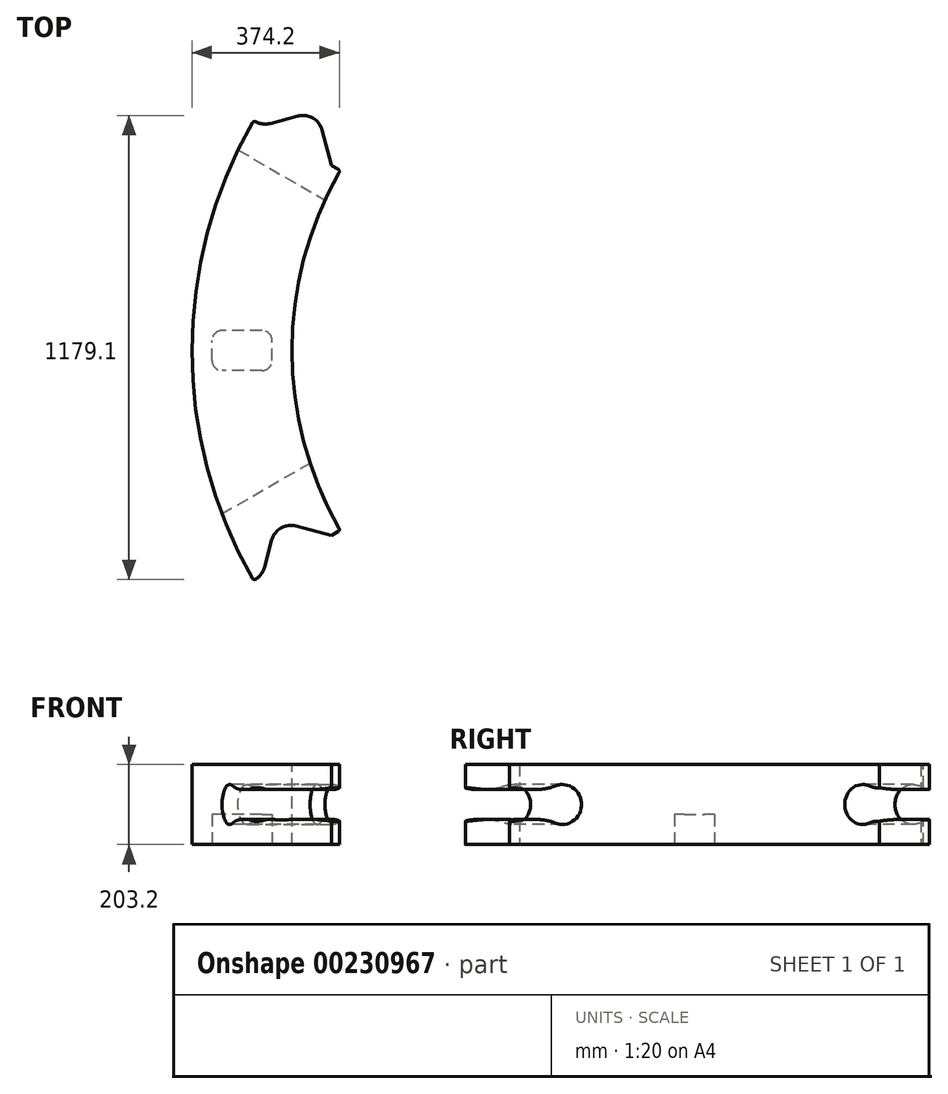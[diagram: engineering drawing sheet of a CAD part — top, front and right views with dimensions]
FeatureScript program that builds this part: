
annotation { "Feature Type Name" : "Feature", "Feature Type Description" : "" }
export const myFeature = defineFeature(function(context is Context, id is Id, definition is map)
    precondition{}
    {
        {
            var Q0;
            Q0=qCreatedBy(makeId("Front.planeOp"),FACE);
            var sketch = newSketch(context, id + "F0", { "sketchPlane" : qUnion([Q0])});
            skLineSegment(sketch, "E0.bottom", {"start": v(-1168.4, 101.6) * mm, "end": v(-914.4, 101.6) * mm});
            skLineSegment(sketch, "E0.top", {"start": v(-1168.4, -101.6) * mm, "end": v(-914.4, -101.6) * mm});
            skLineSegment(sketch, "E0.left", {"start": v(-1168.4, 101.6) * mm, "end": v(-1168.4, -101.6) * mm});
            skLineSegment(sketch, "E0.right", {"start": v(-914.4, 101.6) * mm, "end": v(-914.4, -101.6) * mm});
            skPoint(sketch, "E0.middle", {"position": v(-1041.4, 0) * mm});
            skLineSegment(sketch, "E1", {"start": v(0, 122.44) * mm, "end": v(0, -122.44) * mm, "construction": true});
            skSolve(sketch);
        }
        {
            var Q0;
            Q0=makeQuery(id+"F0.imprint","IMPRINT",FACE,{"disambiguationData":[TD([[makeQuery(id+"F0.imprint","IMPRINT",EDGE,{"derivedFrom":sQuery(id+"F0.wireOp",EDGE,"E0.bottom")}),-1.0]])]});
            var Q1;
            Q1=sQuery(id+"F0.wireOp",EDGE,"E1");
            revolve(context, id + "F1", {"entities" : qUnion([Q0]), "axis" : qUnion([Q1]), "revolveType" : RevolveType.SYMMETRIC, "angle" : 60 * degree});
        }
        {
            var Q0;
            Q0=makeQuery(id+"F1.opRevolve","SWEPT_FACE",FACE,{"disambiguationData":[OSD([sQuery(id+"F0.wireOp",EDGE,"E0.bottom")])]});
            var sketch = newSketch(context, id + "F2", { "sketchPlane" : qUnion([Q0])});
            skLineSegment(sketch, "E2", {"start": v(-989.87, 571.5) * mm, "end": v(-851.08, 608.69) * mm});
            skLineSegment(sketch, "E3", {"start": v(-851.08, 608.69) * mm, "end": v(-813.9, 469.9) * mm});
            skSolve(sketch);
        }
        {
            var Q0;
            Q0=makeQuery(id+"F2.imprint","IMPRINT",FACE,{"disambiguationData":[TD([[makeQuery(id+"F2.imprint","IMPRINT",EDGE,{"derivedFrom":sQuery(id+"F2.wireOp",EDGE,"E2")}),-1.0]])]});
            var Q1;
            Q1=makeQuery(id+"F1.opRevolve","SWEPT_FACE",FACE,{"disambiguationData":[OSD([sQuery(id+"F0.wireOp",EDGE,"E0.top")])]});
            extrude(context, id + "F3", {"entities" : qUnion([Q0]), "operationType" : NewBodyOperationType.ADD, "endBound" : BoundingType.UP_TO_SURFACE, "oppositeDirection" : true, "endBoundEntityFace" : qUnion([Q1]), "depth" : 25.4 * mm});
        }
        {
            var Q0;
            {var subQ0=sQuery(id+"F0.wireOp",EDGE,"E0.bottom");Q0=makeQuery(id+"F3.boolean.opBoolean","MERGE",FACE,{"derivedFrom":[makeQuery(id+"F1.opRevolve","SWEPT_FACE",FACE,{"disambiguationData":[OSD([subQ0])]}),makeQuery(id+"F3.opExtrude","CAP_FACE",FACE,{"disambiguationData":[OSD([subQ0,sQuery(id+"F2.wireOp",EDGE,"E2"),sQuery(id+"F2.wireOp",EDGE,"E3")])],"isStart":true})]});}
            var sketch = newSketch(context, id + "F4", { "sketchPlane" : qUnion([Q0])});
            skLineSegment(sketch, "E4", {"start": v(-989.87, -571.5) * mm, "end": v(-952.68, -432.71) * mm});
            skLineSegment(sketch, "E5", {"start": v(-952.68, -432.71) * mm, "end": v(-813.9, -469.9) * mm});
            skSolve(sketch);
        }
        {
            var Q0;
            Q0=qSketchRegion(id+"F4",true);
            var Q1;
            Q1=makeQuery(id+"F4.imprint","IMPRINT",FACE,{"disambiguationData":[TD([[makeQuery(id+"F4.imprint","IMPRINT",EDGE,{"derivedFrom":sQuery(id+"F4.wireOp",EDGE,"E4")}),-1.0]])]});
            var Q2;
            {var subQ0=sQuery(id+"F0.wireOp",EDGE,"E0.top");Q2=makeQuery(id+"F3.boolean.opBoolean","MERGE",FACE,{"derivedFrom":[makeQuery(id+"F1.opRevolve","SWEPT_FACE",FACE,{"disambiguationData":[OSD([subQ0])]}),makeQuery(id+"F3.opExtrude","CAP_FACE",FACE,{"disambiguationData":[OSD([subQ0])],"isStart":false})]});}
            extrude(context, id + "F5", {"entities" : qUnion([Q0, Q1]), "operationType" : NewBodyOperationType.REMOVE, "endBound" : BoundingType.UP_TO_SURFACE, "oppositeDirection" : true, "endBoundEntityFace" : qUnion([Q2]), "depth" : 25.4 * mm});
        }
        {
            var Q0;
            Q0=makeQuery(id+"F3.opExtrude","SWEPT_EDGE",EDGE,{"disambiguationData":[OSD([sQuery(id+"F2.wireOp",EDGE,"E2"),sQuery(id+"F2.wireOp",EDGE,"E3")])]});
            var Q1;
            Q1=makeQuery(id+"F3.opExtrude","SWEPT_FACE",FACE,{"disambiguationData":[OSD([sQuery(id+"F2.wireOp",EDGE,"E2")])]});
            cPlane(context, id + "F6", {"entities" : qUnion([Q0, Q1]), "cplaneType" : CPlaneType.LINE_ANGLE, "offset" : 25.4 * mm, "angle" : 45 * degree, "width" : 152.4 * mm, "height" : 152.4 * mm});
        }
        {
            var Q0;
            Q0=makeQuery(id+"F5.boolean.opBoolean","COPY",EDGE,{"derivedFrom":makeQuery(id+"F5.opExtrude","SWEPT_EDGE",EDGE,{"disambiguationData":[OSD([sQuery(id+"F4.wireOp",EDGE,"E4"),sQuery(id+"F4.wireOp",EDGE,"E5")])]})});
            var Q1;
            Q1=makeQuery(id+"F5.boolean.opBoolean","COPY",FACE,{"derivedFrom":makeQuery(id+"F5.opExtrude","SWEPT_FACE",FACE,{"disambiguationData":[OSD([sQuery(id+"F4.wireOp",EDGE,"E4")])]})});
            cPlane(context, id + "F7", {"entities" : qUnion([Q0, Q1]), "cplaneType" : CPlaneType.LINE_ANGLE, "offset" : 25.4 * mm, "angle" : 45 * degree, "width" : 152.4 * mm, "height" : 152.4 * mm});
        }
        {
            var Q0;
            Q0=qCreatedBy(id+"F6.planeOp",FACE);
            var sketch = newSketch(context, id + "F8", { "sketchPlane" : qUnion([Q0])});
            skArc(sketch, "E6", {"start": v(-15.92, 47.62) * mm, "mid": v(-84.4, 0) * mm, "end": v(-15.92, -47.63) * mm});
            skArc(sketch, "E7", {"start": v(117.52, -47.63) * mm, "mid": v(186, 0) * mm, "end": v(117.52, 47.62) * mm});
            skLineSegment(sketch, "E8", {"start": v(37.1, 38.1) * mm, "end": v(64.5, 38.1) * mm});
            skLineSegment(sketch, "E9", {"start": v(37.1, -38.1) * mm, "end": v(64.5, -38.1) * mm});
            skPoint(sketch, "E10.visualSharp", {"position": v(0, 38.1) * mm});
            skArc(sketch, "E10.filletArc", {"start": v(-15.92, 47.63) * mm, "mid": v(10.17, 40.5) * mm, "end": v(37.1, 38.1) * mm});
            skPoint(sketch, "E11.visualSharp", {"position": v(101.6, 38.1) * mm});
            skArc(sketch, "E11.filletArc", {"start": v(64.5, 38.1) * mm, "mid": v(91.43, 40.5) * mm, "end": v(117.52, 47.63) * mm});
            skPoint(sketch, "E12.visualSharp", {"position": v(101.6, -38.1) * mm});
            skArc(sketch, "E12.filletArc", {"start": v(117.52, -47.63) * mm, "mid": v(91.43, -40.5) * mm, "end": v(64.5, -38.1) * mm});
            skPoint(sketch, "E13.visualSharp", {"position": v(0, -38.1) * mm});
            skArc(sketch, "E13.filletArc", {"start": v(37.1, -38.1) * mm, "mid": v(10.17, -40.5) * mm, "end": v(-15.92, -47.63) * mm});
            skSolve(sketch);
        }
        {
            var Q0;
            Q0=qSketchRegion(id+"F8",true);
            extrude(context, id + "F9", {"entities" : qUnion([Q0]), "operationType" : NewBodyOperationType.REMOVE, "endBound" : BoundingType.SYMMETRIC, "oppositeDirection" : true, "depth" : 508 * mm});
        }
        {
            var Q0;
            Q0=qCreatedBy(id+"F7.planeOp",FACE);
            var sketch = newSketch(context, id + "F10", { "sketchPlane" : qUnion([Q0])});
            skArc(sketch, "E14", {"start": v(-117.52, 47.63) * mm, "mid": v(-186, 0) * mm, "end": v(-117.52, -47.63) * mm});
            skArc(sketch, "E15", {"start": v(15.92, -47.63) * mm, "mid": v(84.4, 0) * mm, "end": v(15.92, 47.63) * mm});
            skLineSegment(sketch, "E16", {"start": v(-37.1, 38.1) * mm, "end": v(-64.5, 38.1) * mm});
            skLineSegment(sketch, "E17", {"start": v(-37.1, -38.1) * mm, "end": v(-64.5, -38.1) * mm});
            skPoint(sketch, "E18.visualSharp", {"position": v(0, 38.1) * mm});
            skArc(sketch, "E18.filletArc", {"start": v(-37.1, 38.1) * mm, "mid": v(-10.17, 40.5) * mm, "end": v(15.92, 47.63) * mm});
            skPoint(sketch, "E19.visualSharp", {"position": v(-101.6, 38.1) * mm});
            skArc(sketch, "E19.filletArc", {"start": v(-117.52, 47.62) * mm, "mid": v(-91.43, 40.5) * mm, "end": v(-64.5, 38.1) * mm});
            skPoint(sketch, "E20.visualSharp", {"position": v(-101.6, -38.1) * mm});
            skArc(sketch, "E20.filletArc", {"start": v(-64.5, -38.1) * mm, "mid": v(-91.43, -40.5) * mm, "end": v(-117.52, -47.62) * mm});
            skPoint(sketch, "E21.visualSharp", {"position": v(0, -38.1) * mm});
            skArc(sketch, "E21.filletArc", {"start": v(15.92, -47.63) * mm, "mid": v(-10.17, -40.5) * mm, "end": v(-37.1, -38.1) * mm});
            skSolve(sketch);
        }
        {
            var Q0;
            Q0=qSketchRegion(id+"F10",true);
            extrude(context, id + "F11", {"entities" : qUnion([Q0]), "operationType" : NewBodyOperationType.REMOVE, "endBound" : BoundingType.SYMMETRIC, "oppositeDirection" : true, "depth" : 508 * mm});
        }
        {
            var Q0;
            {var subQ0=sQuery(id+"F0.wireOp",EDGE,"E0.top");Q0=makeQuery(id+"F3.boolean.opBoolean","MERGE",FACE,{"derivedFrom":[makeQuery(id+"F1.opRevolve","SWEPT_FACE",FACE,{"disambiguationData":[OSD([subQ0])]}),makeQuery(id+"F3.opExtrude","CAP_FACE",FACE,{"disambiguationData":[OSD([subQ0])],"isStart":false})]});}
            var sketch = newSketch(context, id + "F12", { "sketchPlane" : qUnion([Q0])});
            skLineSegment(sketch, "E22.bottom", {"start": v(-990.6, 50.8) * mm, "end": v(-1092.2, 50.8) * mm});
            skLineSegment(sketch, "E22.top", {"start": v(-990.6, -50.8) * mm, "end": v(-1092.2, -50.8) * mm});
            skLineSegment(sketch, "E22.left", {"start": v(-965.2, 25.4) * mm, "end": v(-965.2, -25.4) * mm});
            skLineSegment(sketch, "E22.right", {"start": v(-1117.6, 25.4) * mm, "end": v(-1117.6, -25.4) * mm});
            skPoint(sketch, "E22.middle", {"position": v(-1041.4, 0) * mm});
            skPoint(sketch, "E23.visualSharp", {"position": v(-965.2, 50.8) * mm});
            skArc(sketch, "E23.filletArc", {"start": v(-965.2, 25.4) * mm, "mid": v(-972.64, 43.36) * mm, "end": v(-990.6, 50.8) * mm});
            skPoint(sketch, "E24.visualSharp", {"position": v(-965.2, -50.8) * mm});
            skArc(sketch, "E24.filletArc", {"start": v(-990.6, -50.8) * mm, "mid": v(-972.64, -43.36) * mm, "end": v(-965.2, -25.4) * mm});
            skPoint(sketch, "E25.visualSharp", {"position": v(-1117.6, -50.8) * mm});
            skArc(sketch, "E25.filletArc", {"start": v(-1117.6, -25.4) * mm, "mid": v(-1110.16, -43.36) * mm, "end": v(-1092.2, -50.8) * mm});
            skPoint(sketch, "E26.visualSharp", {"position": v(-1117.6, 50.8) * mm});
            skArc(sketch, "E26.filletArc", {"start": v(-1092.2, 50.8) * mm, "mid": v(-1110.16, 43.36) * mm, "end": v(-1117.6, 25.4) * mm});
            skSolve(sketch);
        }
        {
            var Q0;
            Q0=qSketchRegion(id+"F12",true);
            extrude(context, id + "F13", {"entities" : qUnion([Q0]), "operationType" : NewBodyOperationType.REMOVE, "oppositeDirection" : true, "depth" : 76.2 * mm});
        }
        {
            var Q0;
            {var subQ0=sQuery(id+"F4.wireOp",EDGE,"E5");var subQ1=sQuery(id+"F0.wireOp",EDGE,"E0.bottom");Q0=makeQuery(id+"F11.boolean.opBoolean","SPLIT",EDGE,{"disambiguationData":[TD([makeQuery(id+"F1.opRevolve","SWEPT_FACE",FACE,{"disambiguationData":[OSD([subQ1])]})])],"derivedFrom":makeQuery(id+"F5.boolean.opBoolean","COPY",EDGE,{"derivedFrom":makeQuery(id+"F5.opExtrude","SWEPT_EDGE",EDGE,{"disambiguationData":[OSD([subQ1,subQ0])]})})});}
            var Q1;
            {var subQ0=sQuery(id+"F4.wireOp",EDGE,"E4");var subQ1=sQuery(id+"F0.wireOp",EDGE,"E0.bottom");Q1=makeQuery(id+"F11.boolean.opBoolean","SPLIT",EDGE,{"disambiguationData":[TD([makeQuery(id+"F1.opRevolve","SWEPT_FACE",FACE,{"disambiguationData":[OSD([subQ1])]})])],"derivedFrom":makeQuery(id+"F5.boolean.opBoolean","COPY",EDGE,{"derivedFrom":makeQuery(id+"F5.opExtrude","SWEPT_EDGE",EDGE,{"disambiguationData":[OSD([subQ1,subQ0])]})})});}
            var Q2;
            {var subQ0=sQuery(id+"F4.wireOp",EDGE,"E4");var subQ1=sQuery(id+"F0.wireOp",EDGE,"E0.top");var subQ2=sQuery(id+"F0.wireOp",EDGE,"E0.bottom");Q2=makeQuery(id+"F11.boolean.opBoolean","SPLIT",EDGE,{"disambiguationData":[TD([makeQuery(id+"F1.opRevolve","SWEPT_FACE",FACE,{"disambiguationData":[OSD([subQ1])]})])],"derivedFrom":makeQuery(id+"F5.boolean.opBoolean","COPY",EDGE,{"derivedFrom":makeQuery(id+"F5.opExtrude","SWEPT_EDGE",EDGE,{"disambiguationData":[OSD([subQ2,subQ0])]})})});}
            var Q3;
            {var subQ0=sQuery(id+"F4.wireOp",EDGE,"E5");var subQ1=sQuery(id+"F0.wireOp",EDGE,"E0.top");var subQ2=sQuery(id+"F0.wireOp",EDGE,"E0.bottom");Q3=makeQuery(id+"F11.boolean.opBoolean","SPLIT",EDGE,{"disambiguationData":[TD([makeQuery(id+"F1.opRevolve","SWEPT_FACE",FACE,{"disambiguationData":[OSD([subQ1])]})])],"derivedFrom":makeQuery(id+"F5.boolean.opBoolean","COPY",EDGE,{"derivedFrom":makeQuery(id+"F5.opExtrude","SWEPT_EDGE",EDGE,{"disambiguationData":[OSD([subQ2,subQ0])]})})});}
            var Q4;
            {var subQ0=sQuery(id+"F0.wireOp",EDGE,"E0.bottom");var subQ1=sQuery(id+"F2.wireOp",EDGE,"E3");Q4=makeQuery(id+"F9.boolean.opBoolean","SPLIT",EDGE,{"disambiguationData":[TD([makeQuery(id+"F1.opRevolve","SWEPT_FACE",FACE,{"disambiguationData":[OSD([subQ0])]})])],"derivedFrom":makeQuery(id+"F3.opExtrude","SWEPT_EDGE",EDGE,{"disambiguationData":[OSD([subQ0,subQ1])]})});}
            var Q5;
            {var subQ0=sQuery(id+"F0.wireOp",EDGE,"E0.bottom");var subQ1=sQuery(id+"F2.wireOp",EDGE,"E2");Q5=makeQuery(id+"F9.boolean.opBoolean","SPLIT",EDGE,{"disambiguationData":[TD([makeQuery(id+"F1.opRevolve","SWEPT_FACE",FACE,{"disambiguationData":[OSD([subQ0])]})])],"derivedFrom":makeQuery(id+"F3.opExtrude","SWEPT_EDGE",EDGE,{"disambiguationData":[OSD([subQ0,subQ1])]})});}
            var Q6;
            {var subQ0=sQuery(id+"F2.wireOp",EDGE,"E2");var subQ1=sQuery(id+"F0.wireOp",EDGE,"E0.top");var subQ2=sQuery(id+"F0.wireOp",EDGE,"E0.bottom");Q6=makeQuery(id+"F9.boolean.opBoolean","SPLIT",EDGE,{"disambiguationData":[TD([makeQuery(id+"F1.opRevolve","SWEPT_FACE",FACE,{"disambiguationData":[OSD([subQ1])]})])],"derivedFrom":makeQuery(id+"F3.opExtrude","SWEPT_EDGE",EDGE,{"disambiguationData":[OSD([subQ2,subQ0])]})});}
            var Q7;
            {var subQ0=sQuery(id+"F2.wireOp",EDGE,"E3");var subQ1=sQuery(id+"F0.wireOp",EDGE,"E0.top");var subQ2=sQuery(id+"F0.wireOp",EDGE,"E0.bottom");Q7=makeQuery(id+"F9.boolean.opBoolean","SPLIT",EDGE,{"disambiguationData":[TD([makeQuery(id+"F1.opRevolve","SWEPT_FACE",FACE,{"disambiguationData":[OSD([subQ1])]})])],"derivedFrom":makeQuery(id+"F3.opExtrude","SWEPT_EDGE",EDGE,{"disambiguationData":[OSD([subQ2,subQ0])]})});}
            fillet(context, id + "F14", {"entities" : qUnion([Q0, Q1, Q2, Q3, Q4, Q5, Q6, Q7]), "radius" : 50.8 * mm, "tangentPropagation" : true, "allowEdgeOverflow" : false});
        }
        {
            var Q0;
            {var subQ0=sQuery(id+"F4.wireOp",EDGE,"E5");var subQ1=sQuery(id+"F4.wireOp",EDGE,"E4");var subQ2=sQuery(id+"F0.wireOp",EDGE,"E0.bottom");Q0=makeQuery(id+"F11.boolean.opBoolean","SPLIT",EDGE,{"disambiguationData":[TD([makeQuery(id+"F1.opRevolve","SWEPT_FACE",FACE,{"disambiguationData":[OSD([subQ2])]})])],"derivedFrom":makeQuery(id+"F5.boolean.opBoolean","COPY",EDGE,{"derivedFrom":makeQuery(id+"F5.opExtrude","SWEPT_EDGE",EDGE,{"disambiguationData":[OSD([subQ1,subQ0])]})})});}
            var Q1;
            {var subQ0=sQuery(id+"F4.wireOp",EDGE,"E5");var subQ1=sQuery(id+"F0.wireOp",EDGE,"E0.top");var subQ2=sQuery(id+"F4.wireOp",EDGE,"E4");Q1=makeQuery(id+"F11.boolean.opBoolean","SPLIT",EDGE,{"disambiguationData":[TD([makeQuery(id+"F1.opRevolve","SWEPT_FACE",FACE,{"disambiguationData":[OSD([subQ1])]})])],"derivedFrom":makeQuery(id+"F5.boolean.opBoolean","COPY",EDGE,{"derivedFrom":makeQuery(id+"F5.opExtrude","SWEPT_EDGE",EDGE,{"disambiguationData":[OSD([subQ2,subQ0])]})})});}
            var Q2;
            {var subQ0=sQuery(id+"F2.wireOp",EDGE,"E3");var subQ1=sQuery(id+"F2.wireOp",EDGE,"E2");var subQ2=sQuery(id+"F0.wireOp",EDGE,"E0.bottom");Q2=makeQuery(id+"F9.boolean.opBoolean","SPLIT",EDGE,{"disambiguationData":[TD([makeQuery(id+"F1.opRevolve","SWEPT_FACE",FACE,{"disambiguationData":[OSD([subQ2])]})])],"derivedFrom":makeQuery(id+"F3.opExtrude","SWEPT_EDGE",EDGE,{"disambiguationData":[OSD([subQ1,subQ0])]})});}
            var Q3;
            {var subQ0=sQuery(id+"F2.wireOp",EDGE,"E3");var subQ1=sQuery(id+"F2.wireOp",EDGE,"E2");var subQ2=sQuery(id+"F0.wireOp",EDGE,"E0.top");Q3=makeQuery(id+"F9.boolean.opBoolean","SPLIT",EDGE,{"disambiguationData":[TD([makeQuery(id+"F1.opRevolve","SWEPT_FACE",FACE,{"disambiguationData":[OSD([subQ2])]})])],"derivedFrom":makeQuery(id+"F3.opExtrude","SWEPT_EDGE",EDGE,{"disambiguationData":[OSD([subQ1,subQ0])]})});}
            fillet(context, id + "F15", {"entities" : qUnion([Q0, Q1, Q2, Q3]), "radius" : 50.8 * mm, "tangentPropagation" : true, "allowEdgeOverflow" : false});
        }
        {
            var Q0;
            {var subQ0=sQuery(id+"F0.wireOp",EDGE,"E0.right");var subQ1=sQuery(id+"F0.wireOp",EDGE,"E0.bottom");Q0=makeQuery(id+"F11.boolean.opBoolean","SPLIT",EDGE,{"disambiguationData":[TD([makeQuery(id+"F1.opRevolve","SWEPT_FACE",FACE,{"disambiguationData":[OSD([subQ1])]})])],"derivedFrom":makeQuery(id+"F1.opRevolve","CAP_EDGE",EDGE,{"disambiguationData":[OSD([subQ0])],"isStart":true})});}
            var Q1;
            {var subQ0=sQuery(id+"F0.wireOp",EDGE,"E0.right");var subQ1=sQuery(id+"F0.wireOp",EDGE,"E0.top");Q1=makeQuery(id+"F11.boolean.opBoolean","SPLIT",EDGE,{"disambiguationData":[TD([makeQuery(id+"F1.opRevolve","SWEPT_FACE",FACE,{"disambiguationData":[OSD([subQ1])]})])],"derivedFrom":makeQuery(id+"F1.opRevolve","CAP_EDGE",EDGE,{"disambiguationData":[OSD([subQ0])],"isStart":true})});}
            var Q2;
            {var subQ0=sQuery(id+"F0.wireOp",EDGE,"E0.left");var subQ1=sQuery(id+"F0.wireOp",EDGE,"E0.bottom");Q2=makeQuery(id+"F11.boolean.opBoolean","SPLIT",EDGE,{"disambiguationData":[TD([makeQuery(id+"F1.opRevolve","SWEPT_FACE",FACE,{"disambiguationData":[OSD([subQ1])]})])],"derivedFrom":makeQuery(id+"F1.opRevolve","CAP_EDGE",EDGE,{"disambiguationData":[OSD([subQ0])],"isStart":true})});}
            var Q3;
            {var subQ0=sQuery(id+"F0.wireOp",EDGE,"E0.left");var subQ1=sQuery(id+"F0.wireOp",EDGE,"E0.top");Q3=makeQuery(id+"F11.boolean.opBoolean","SPLIT",EDGE,{"disambiguationData":[TD([makeQuery(id+"F1.opRevolve","SWEPT_FACE",FACE,{"disambiguationData":[OSD([subQ1])]})])],"derivedFrom":makeQuery(id+"F1.opRevolve","CAP_EDGE",EDGE,{"disambiguationData":[OSD([subQ0])],"isStart":true})});}
            var Q4;
            {var subQ0=sQuery(id+"F0.wireOp",EDGE,"E0.right");var subQ1=sQuery(id+"F0.wireOp",EDGE,"E0.bottom");Q4=makeQuery(id+"F9.boolean.opBoolean","SPLIT",EDGE,{"disambiguationData":[TD([makeQuery(id+"F1.opRevolve","SWEPT_FACE",FACE,{"disambiguationData":[OSD([subQ1])]})])],"derivedFrom":makeQuery(id+"F1.opRevolve","CAP_EDGE",EDGE,{"disambiguationData":[OSD([subQ0])],"isStart":false})});}
            var Q5;
            {var subQ0=sQuery(id+"F0.wireOp",EDGE,"E0.top");var subQ1=sQuery(id+"F0.wireOp",EDGE,"E0.right");Q5=makeQuery(id+"F9.boolean.opBoolean","SPLIT",EDGE,{"disambiguationData":[TD([makeQuery(id+"F1.opRevolve","SWEPT_FACE",FACE,{"disambiguationData":[OSD([subQ0])]})])],"derivedFrom":makeQuery(id+"F1.opRevolve","CAP_EDGE",EDGE,{"disambiguationData":[OSD([subQ1])],"isStart":false})});}
            var Q6;
            {var subQ0=sQuery(id+"F0.wireOp",EDGE,"E0.left");var subQ1=sQuery(id+"F0.wireOp",EDGE,"E0.bottom");Q6=makeQuery(id+"F9.boolean.opBoolean","SPLIT",EDGE,{"disambiguationData":[TD([makeQuery(id+"F1.opRevolve","SWEPT_FACE",FACE,{"disambiguationData":[OSD([subQ1])]})])],"derivedFrom":makeQuery(id+"F1.opRevolve","CAP_EDGE",EDGE,{"disambiguationData":[OSD([subQ0])],"isStart":false})});}
            var Q7;
            {var subQ0=sQuery(id+"F0.wireOp",EDGE,"E0.top");var subQ1=sQuery(id+"F0.wireOp",EDGE,"E0.left");Q7=makeQuery(id+"F9.boolean.opBoolean","SPLIT",EDGE,{"disambiguationData":[TD([makeQuery(id+"F1.opRevolve","SWEPT_FACE",FACE,{"disambiguationData":[OSD([subQ0])]})])],"derivedFrom":makeQuery(id+"F1.opRevolve","CAP_EDGE",EDGE,{"disambiguationData":[OSD([subQ1])],"isStart":false})});}
            fillet(context, id + "F16", {"entities" : qUnion([Q0, Q1, Q2, Q3, Q4, Q5, Q6, Q7]), "radius" : 6.35 * mm, "tangentPropagation" : true, "allowEdgeOverflow" : false});
        }
    });
